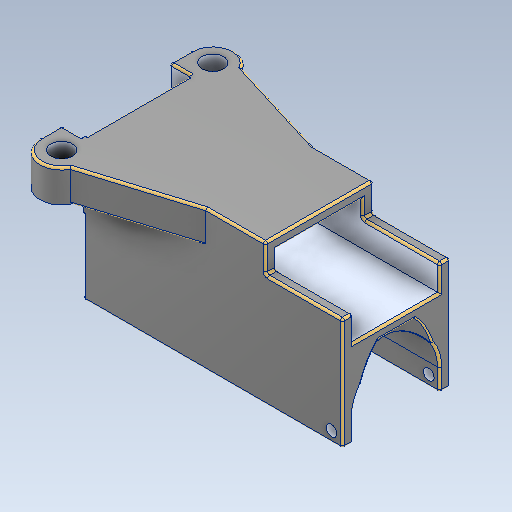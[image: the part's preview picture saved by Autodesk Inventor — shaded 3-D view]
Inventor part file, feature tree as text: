
AUTODESK INVENTOR PART (.ipt)
format: ipt  version: 2021 (Build 250183000, 183)  size: 269,312 bytes
history: mixed  units: mm
features: other x1, fillet x1, imported_body x1
ambient origin geometry x8: Origin, YZ Plane, XZ Plane, XY Plane, X Axis, Y Axis, Z Axis, Center Point
bodies: Body1 (imported_parasolid)
feature tree (3):
  other  "Sólido1"
  fillet  "Redondeo7"  [1 undecoded]
  imported_body  NMx_Import_Brep_tag  [imported B-rep: ~6 faces, bbox_mm=None]
note: 1 required parameter value undecoded (feature->parameter linkage not recoverable at this tier; creation-order binding heuristic only, values carry confidence <= 0.55)
